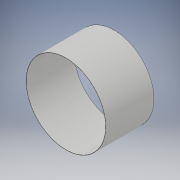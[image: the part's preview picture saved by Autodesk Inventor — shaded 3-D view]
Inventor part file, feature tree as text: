
AUTODESK INVENTOR PART (.ipt)
format: ipt  version: 2019 (Build 230136000, 136)  size: 103,424 bytes
history: native  units: mm
features: extrude x2, sketch x2
ambient origin geometry x8: Origin, YZ Plane, XZ Plane, XY Plane, X Axis, Y Axis, Z Axis, Center Point
bodies: Solid1 (feature_tree)
feature tree (4):
  extrude  "Extrusion1"  Depth=12.06mm TaperAngle=0.0deg
  extrude  "Extrusion2"  Depth=12.06mm TaperAngle=0.0deg
  sketch  "Sketch1"  dims[d0=19.97mm d1=12.06mm d2=0.0mm]
  sketch  "Sketch2"  dims[d3=19.87mm d4=12.06mm d5=0.0mm]
